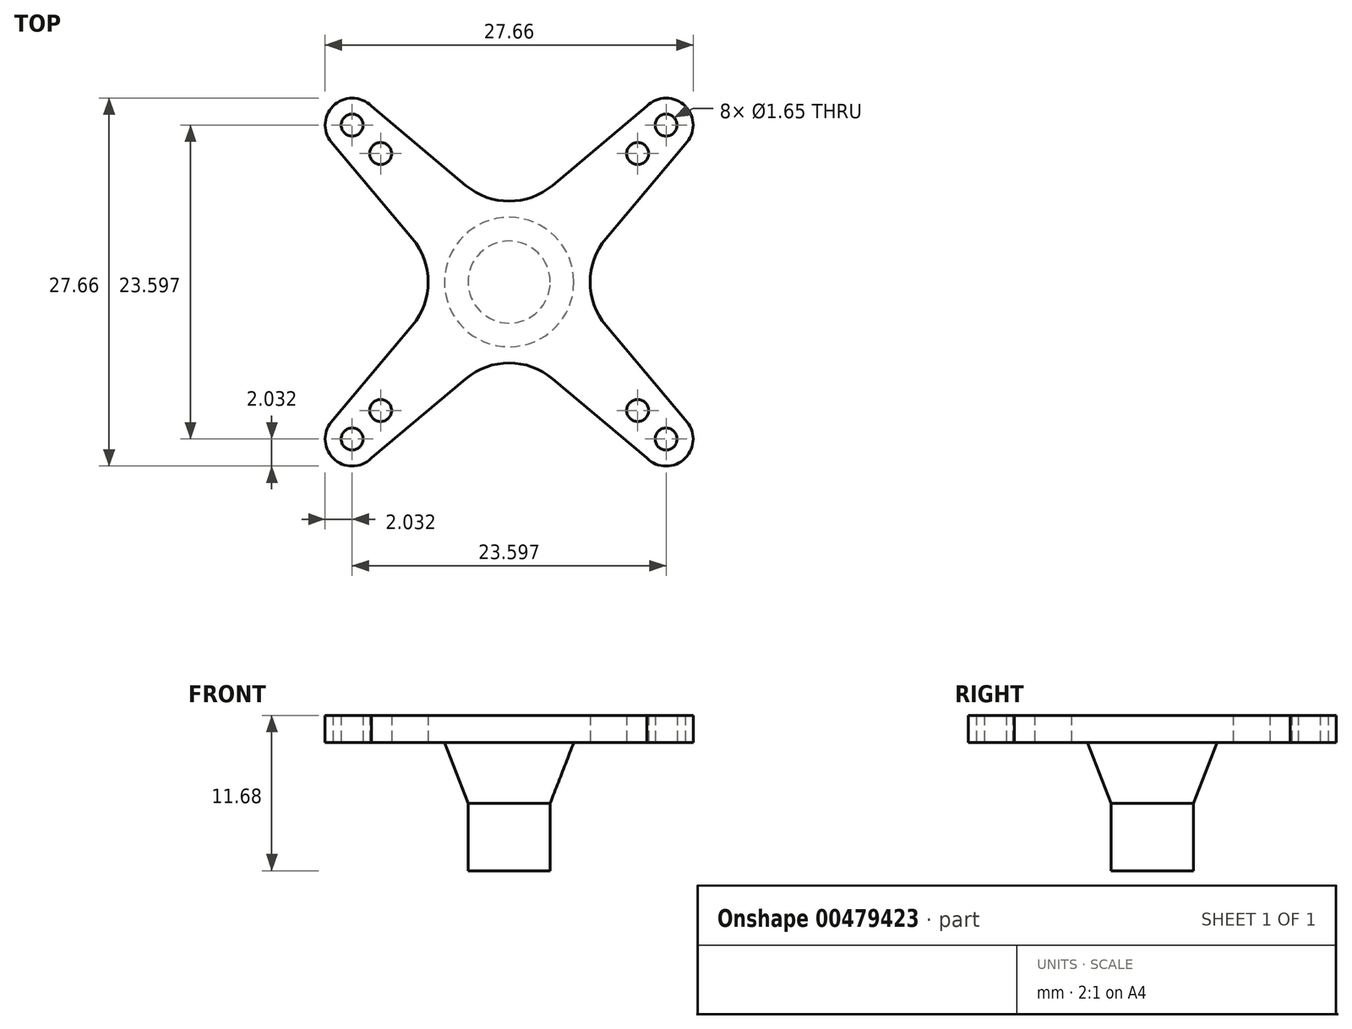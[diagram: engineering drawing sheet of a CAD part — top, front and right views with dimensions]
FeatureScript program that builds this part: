
annotation { "Feature Type Name" : "Feature", "Feature Type Description" : "" }
export const myFeature = defineFeature(function(context is Context, id is Id, definition is map)
    precondition{}
    {
        {
            var Q0;
            Q0=qCreatedBy(makeId("Top.planeOp"),FACE);
            var sketch = newSketch(context, id + "F0", { "sketchPlane" : qUnion([Q0]), "disableImprinting" : false});
            skLineSegment(sketch, "E0", {"start": v(0, 11.16) * mm, "end": v(0, -11.16) * mm});
            skLineSegment(sketch, "E1", {"start": v(11.16, 0) * mm, "end": v(-11.16, 0) * mm});
            skPoint(sketch, "E2", {"position": v(0, 0) * mm});
            skCircle(sketch, "E3", {"center": v(0, 11.16) * mm, "radius": 5.08 * mm});
            skCircle(sketch, "E4", {"center": v(11.16, 0) * mm, "radius": 5.08 * mm});
            skCircle(sketch, "E5", {"center": v(0, -11.16) * mm, "radius": 5.08 * mm});
            skCircle(sketch, "E6", {"center": v(-11.16, 0) * mm, "radius": 5.08 * mm});
            skLineSegment(sketch, "E7", {"start": v(-3.26, 7.27) * mm, "end": v(3.26, 7.27) * mm});
            skLineSegment(sketch, "E8", {"start": v(7.27, 3.26) * mm, "end": v(7.27, -3.26) * mm});
            skLineSegment(sketch, "E9", {"start": v(-3.26, -7.27) * mm, "end": v(3.26, -7.27) * mm});
            skLineSegment(sketch, "E10", {"start": v(-7.27, 3.26) * mm, "end": v(-7.27, -3.26) * mm});
            skLineSegment(sketch, "E11", {"start": v(3.26, -7.27) * mm, "end": v(10.36, -13.24) * mm});
            skLineSegment(sketch, "E12", {"start": v(7.27, -3.26) * mm, "end": v(13.24, -10.36) * mm});
            skLineSegment(sketch, "E13", {"start": v(3.26, 7.27) * mm, "end": v(10.36, 13.24) * mm});
            skLineSegment(sketch, "E14", {"start": v(7.27, 3.26) * mm, "end": v(13.24, 10.36) * mm});
            skLineSegment(sketch, "E15", {"start": v(-7.27, -3.26) * mm, "end": v(-13.24, -10.36) * mm});
            skLineSegment(sketch, "E16", {"start": v(-3.26, -7.27) * mm, "end": v(-10.36, -13.24) * mm});
            skLineSegment(sketch, "E17", {"start": v(-7.27, 3.26) * mm, "end": v(-13.24, 10.36) * mm});
            skLineSegment(sketch, "E18", {"start": v(-3.26, 7.27) * mm, "end": v(-10.36, 13.24) * mm});
            skLineSegment(sketch, "E19", {"start": v(-13.24, 10.36) * mm, "end": v(-10.36, 13.24) * mm});
            skLineSegment(sketch, "E20", {"start": v(10.36, 13.24) * mm, "end": v(13.24, 10.36) * mm});
            skLineSegment(sketch, "E21", {"start": v(13.24, -10.36) * mm, "end": v(10.36, -13.24) * mm});
            skLineSegment(sketch, "E22", {"start": v(-10.36, -13.24) * mm, "end": v(-13.24, -10.36) * mm});
            skPoint(sketch, "E23", {"position": v(-11.8, 11.8) * mm});
            skPoint(sketch, "E24", {"position": v(11.8, 11.8) * mm});
            skPoint(sketch, "E25", {"position": v(11.8, -11.8) * mm});
            skPoint(sketch, "E26", {"position": v(-11.8, -11.8) * mm});
            skCircle(sketch, "E27", {"center": v(-11.8, 11.8) * mm, "radius": 2.03 * mm});
            skCircle(sketch, "E28", {"center": v(11.8, 11.8) * mm, "radius": 2.03 * mm});
            skCircle(sketch, "E29", {"center": v(11.8, -11.8) * mm, "radius": 2.03 * mm});
            skCircle(sketch, "E30", {"center": v(-11.8, -11.8) * mm, "radius": 2.03 * mm});
            skLineSegment(sketch, "E31", {"start": v(-3.26, 7.27) * mm, "end": v(-7.27, 3.26) * mm});
            skLineSegment(sketch, "E32", {"start": v(3.26, 7.27) * mm, "end": v(7.27, 3.26) * mm});
            skLineSegment(sketch, "E33", {"start": v(7.27, -3.26) * mm, "end": v(3.26, -7.27) * mm});
            skLineSegment(sketch, "E34", {"start": v(-7.27, -3.26) * mm, "end": v(-3.26, -7.27) * mm});
            skLineSegment(sketch, "E35", {"start": v(-11.8, 11.8) * mm, "end": v(-5.27, 5.27) * mm});
            skLineSegment(sketch, "E36", {"start": v(11.8, 11.8) * mm, "end": v(5.27, 5.27) * mm});
            skLineSegment(sketch, "E37", {"start": v(11.8, -11.8) * mm, "end": v(5.27, -5.27) * mm});
            skLineSegment(sketch, "E38", {"start": v(-11.8, -11.8) * mm, "end": v(-5.27, -5.27) * mm});
            skCircle(sketch, "E39", {"center": v(-11.8, 11.8) * mm, "radius": 0.83 * mm});
            skCircle(sketch, "E40", {"center": v(11.8, 11.8) * mm, "radius": 0.83 * mm});
            skCircle(sketch, "E41", {"center": v(11.8, -11.8) * mm, "radius": 0.83 * mm});
            skCircle(sketch, "E42", {"center": v(-11.8, -11.8) * mm, "radius": 0.83 * mm});
            skCircle(sketch, "E43", {"center": v(-9.66, 9.66) * mm, "radius": 0.83 * mm});
            skCircle(sketch, "E44", {"center": v(9.66, 9.66) * mm, "radius": 0.83 * mm});
            skCircle(sketch, "E45", {"center": v(-9.66, -9.66) * mm, "radius": 0.83 * mm});
            skCircle(sketch, "E46", {"center": v(9.66, -9.66) * mm, "radius": 0.83 * mm});
            skCircle(sketch, "E47", {"center": v(0, 0) * mm, "radius": 4.86 * mm});
            skSolve(sketch);
        }
        {
            var Q0;
            {var subQ1=sQuery(id+"F0.wireOp",EDGE,"E19");var subQ3=sQuery(id+"F0.wireOp",EDGE,"E39");var subQ4=makeQuery(id+"F0.imprint","INTERSECT",VERTEX,{"disambiguationData":[OD(0.0)],"derivedFrom":[subQ1,subQ3]});Q0=makeQuery(id+"F0.imprint","IMPRINT",FACE,{"disambiguationData":[TD([[makeQuery(id+"F0.imprint","IMPRINT",EDGE,{"disambiguationData":[TD([[subQ4,1.0]])],"derivedFrom":subQ3}),-1.0]])]});}
            var Q1;
            {var subQ1=sQuery(id+"F0.wireOp",EDGE,"E20");var subQ3=sQuery(id+"F0.wireOp",EDGE,"E40");var subQ4=makeQuery(id+"F0.imprint","INTERSECT",VERTEX,{"disambiguationData":[OD(0.0)],"derivedFrom":[subQ1,subQ3]});Q1=makeQuery(id+"F0.imprint","IMPRINT",FACE,{"disambiguationData":[TD([[makeQuery(id+"F0.imprint","IMPRINT",EDGE,{"disambiguationData":[TD([[subQ4,1.0]])],"derivedFrom":subQ3}),-1.0]])]});}
            var Q2;
            {var subQ1=sQuery(id+"F0.wireOp",EDGE,"E21");var subQ3=sQuery(id+"F0.wireOp",EDGE,"E41");var subQ4=makeQuery(id+"F0.imprint","INTERSECT",VERTEX,{"disambiguationData":[OD(0.0)],"derivedFrom":[subQ1,subQ3]});Q2=makeQuery(id+"F0.imprint","IMPRINT",FACE,{"disambiguationData":[TD([[makeQuery(id+"F0.imprint","IMPRINT",EDGE,{"disambiguationData":[TD([[subQ4,1.0]])],"derivedFrom":subQ3}),-1.0]])]});}
            var Q3;
            {var subQ1=sQuery(id+"F0.wireOp",EDGE,"E22");var subQ3=sQuery(id+"F0.wireOp",EDGE,"E42");var subQ4=makeQuery(id+"F0.imprint","INTERSECT",VERTEX,{"disambiguationData":[OD(0.0)],"derivedFrom":[subQ1,subQ3]});Q3=makeQuery(id+"F0.imprint","IMPRINT",FACE,{"disambiguationData":[TD([[makeQuery(id+"F0.imprint","IMPRINT",EDGE,{"disambiguationData":[TD([[subQ4,1.0]])],"derivedFrom":subQ3}),-1.0]])]});}
            var Q4;
            {var subQ0=sQuery(id+"F0.wireOp",EDGE,"E27");var subQ5=sQuery(id+"F0.wireOp",EDGE,"E35");var subQ6=makeQuery(id+"F0.imprint","INTERSECT",VERTEX,{"derivedFrom":[subQ0,subQ5]});Q4=makeQuery(id+"F0.imprint","IMPRINT",FACE,{"disambiguationData":[TD([[makeQuery(id+"F0.imprint","IMPRINT",EDGE,{"disambiguationData":[TD([[subQ6,1.0]])],"derivedFrom":subQ5}),-1.0]])]});}
            var Q5;
            {var subQ0=sQuery(id+"F0.wireOp",EDGE,"E27");var subQ5=sQuery(id+"F0.wireOp",EDGE,"E35");var subQ6=makeQuery(id+"F0.imprint","INTERSECT",VERTEX,{"derivedFrom":[subQ0,subQ5]});Q5=makeQuery(id+"F0.imprint","IMPRINT",FACE,{"disambiguationData":[TD([[makeQuery(id+"F0.imprint","IMPRINT",EDGE,{"disambiguationData":[TD([[subQ6,1.0]])],"derivedFrom":subQ5}),1.0]])]});}
            var Q6;
            {var subQ0=sQuery(id+"F0.wireOp",EDGE,"E28");var subQ5=sQuery(id+"F0.wireOp",EDGE,"E36");var subQ6=makeQuery(id+"F0.imprint","INTERSECT",VERTEX,{"derivedFrom":[subQ0,subQ5]});Q6=makeQuery(id+"F0.imprint","IMPRINT",FACE,{"disambiguationData":[TD([[makeQuery(id+"F0.imprint","IMPRINT",EDGE,{"disambiguationData":[TD([[subQ6,1.0]])],"derivedFrom":subQ5}),-1.0]])]});}
            var Q7;
            {var subQ0=sQuery(id+"F0.wireOp",EDGE,"E28");var subQ5=sQuery(id+"F0.wireOp",EDGE,"E36");var subQ6=makeQuery(id+"F0.imprint","INTERSECT",VERTEX,{"derivedFrom":[subQ0,subQ5]});Q7=makeQuery(id+"F0.imprint","IMPRINT",FACE,{"disambiguationData":[TD([[makeQuery(id+"F0.imprint","IMPRINT",EDGE,{"disambiguationData":[TD([[subQ6,1.0]])],"derivedFrom":subQ5}),1.0]])]});}
            var Q8;
            {var subQ0=sQuery(id+"F0.wireOp",EDGE,"E29");var subQ5=sQuery(id+"F0.wireOp",EDGE,"E37");var subQ6=makeQuery(id+"F0.imprint","INTERSECT",VERTEX,{"derivedFrom":[subQ0,subQ5]});Q8=makeQuery(id+"F0.imprint","IMPRINT",FACE,{"disambiguationData":[TD([[makeQuery(id+"F0.imprint","IMPRINT",EDGE,{"disambiguationData":[TD([[subQ6,1.0]])],"derivedFrom":subQ5}),-1.0]])]});}
            var Q9;
            {var subQ0=sQuery(id+"F0.wireOp",EDGE,"E29");var subQ5=sQuery(id+"F0.wireOp",EDGE,"E37");var subQ6=makeQuery(id+"F0.imprint","INTERSECT",VERTEX,{"derivedFrom":[subQ0,subQ5]});Q9=makeQuery(id+"F0.imprint","IMPRINT",FACE,{"disambiguationData":[TD([[makeQuery(id+"F0.imprint","IMPRINT",EDGE,{"disambiguationData":[TD([[subQ6,1.0]])],"derivedFrom":subQ5}),1.0]])]});}
            var Q10;
            {var subQ0=sQuery(id+"F0.wireOp",EDGE,"E30");var subQ5=sQuery(id+"F0.wireOp",EDGE,"E38");var subQ6=makeQuery(id+"F0.imprint","INTERSECT",VERTEX,{"derivedFrom":[subQ0,subQ5]});Q10=makeQuery(id+"F0.imprint","IMPRINT",FACE,{"disambiguationData":[TD([[makeQuery(id+"F0.imprint","IMPRINT",EDGE,{"disambiguationData":[TD([[subQ6,1.0]])],"derivedFrom":subQ5}),-1.0]])]});}
            var Q11;
            {var subQ0=sQuery(id+"F0.wireOp",EDGE,"E30");var subQ5=sQuery(id+"F0.wireOp",EDGE,"E38");var subQ6=makeQuery(id+"F0.imprint","INTERSECT",VERTEX,{"derivedFrom":[subQ0,subQ5]});Q11=makeQuery(id+"F0.imprint","IMPRINT",FACE,{"disambiguationData":[TD([[makeQuery(id+"F0.imprint","IMPRINT",EDGE,{"disambiguationData":[TD([[subQ6,1.0]])],"derivedFrom":subQ5}),1.0]])]});}
            var Q12;
            {var subQ6=sQuery(id+"F0.wireOp",EDGE,"E18");Q12=makeQuery(id+"F0.imprint","IMPRINT",FACE,{"disambiguationData":[TD([[makeQuery(id+"F0.imprint","IMPRINT",EDGE,{"derivedFrom":subQ6}),1.0]])]});}
            var Q13;
            {var subQ6=sQuery(id+"F0.wireOp",EDGE,"E13");Q13=makeQuery(id+"F0.imprint","IMPRINT",FACE,{"disambiguationData":[TD([[makeQuery(id+"F0.imprint","IMPRINT",EDGE,{"derivedFrom":subQ6}),-1.0]])]});}
            var Q14;
            {var subQ6=sQuery(id+"F0.wireOp",EDGE,"E14");Q14=makeQuery(id+"F0.imprint","IMPRINT",FACE,{"disambiguationData":[TD([[makeQuery(id+"F0.imprint","IMPRINT",EDGE,{"derivedFrom":subQ6}),1.0]])]});}
            var Q15;
            {var subQ0=sQuery(id+"F0.wireOp",EDGE,"E12");Q15=makeQuery(id+"F0.imprint","IMPRINT",FACE,{"disambiguationData":[TD([[makeQuery(id+"F0.imprint","IMPRINT",EDGE,{"derivedFrom":subQ0}),-1.0]])]});}
            var Q16;
            {var subQ6=sQuery(id+"F0.wireOp",EDGE,"E11");Q16=makeQuery(id+"F0.imprint","IMPRINT",FACE,{"disambiguationData":[TD([[makeQuery(id+"F0.imprint","IMPRINT",EDGE,{"derivedFrom":subQ6}),1.0]])]});}
            var Q17;
            {var subQ6=sQuery(id+"F0.wireOp",EDGE,"E16");Q17=makeQuery(id+"F0.imprint","IMPRINT",FACE,{"disambiguationData":[TD([[makeQuery(id+"F0.imprint","IMPRINT",EDGE,{"derivedFrom":subQ6}),-1.0]])]});}
            var Q18;
            {var subQ8=sQuery(id+"F0.wireOp",EDGE,"E17");Q18=makeQuery(id+"F0.imprint","IMPRINT",FACE,{"disambiguationData":[TD([[makeQuery(id+"F0.imprint","IMPRINT",EDGE,{"derivedFrom":subQ8}),-1.0]])]});}
            var Q19;
            {var subQ6=sQuery(id+"F0.wireOp",EDGE,"E15");Q19=makeQuery(id+"F0.imprint","IMPRINT",FACE,{"disambiguationData":[TD([[makeQuery(id+"F0.imprint","IMPRINT",EDGE,{"derivedFrom":subQ6}),1.0]])]});}
            var Q20;
            {var subQ5=sQuery(id+"F0.wireOp",EDGE,"E3");var subQ7=sQuery(id+"F0.wireOp",EDGE,"E0");var subQ8=makeQuery(id+"F0.imprint","INTERSECT",VERTEX,{"derivedFrom":[subQ7,subQ5]});Q20=makeQuery(id+"F0.imprint","IMPRINT",FACE,{"disambiguationData":[TD([[makeQuery(id+"F0.imprint","IMPRINT",EDGE,{"disambiguationData":[TD([[subQ8,-1.0]])],"derivedFrom":subQ7}),1.0]])]});}
            var Q21;
            {var subQ5=sQuery(id+"F0.wireOp",EDGE,"E3");var subQ6=sQuery(id+"F0.wireOp",EDGE,"E0");var subQ7=makeQuery(id+"F0.imprint","INTERSECT",VERTEX,{"derivedFrom":[subQ6,subQ5]});Q21=makeQuery(id+"F0.imprint","IMPRINT",FACE,{"disambiguationData":[TD([[makeQuery(id+"F0.imprint","IMPRINT",EDGE,{"disambiguationData":[TD([[subQ7,-1.0]])],"derivedFrom":subQ6}),-1.0]])]});}
            var Q22;
            {var subQ3=sQuery(id+"F0.wireOp",EDGE,"E0");var subQ5=sQuery(id+"F0.wireOp",EDGE,"E1");var subQ6=makeQuery(id+"F0.imprint","INTERSECT",VERTEX,{"derivedFrom":[subQ3,subQ5]});Q22=makeQuery(id+"F0.imprint","IMPRINT",FACE,{"disambiguationData":[TD([[makeQuery(id+"F0.imprint","IMPRINT",EDGE,{"disambiguationData":[TD([[subQ6,-1.0]])],"derivedFrom":subQ3}),-1.0]])]});}
            var Q23;
            {var subQ3=sQuery(id+"F0.wireOp",EDGE,"E0");var subQ7=sQuery(id+"F0.wireOp",EDGE,"E1");var subQ9=makeQuery(id+"F0.imprint","INTERSECT",VERTEX,{"derivedFrom":[subQ3,subQ7]});Q23=makeQuery(id+"F0.imprint","IMPRINT",FACE,{"disambiguationData":[TD([[makeQuery(id+"F0.imprint","IMPRINT",EDGE,{"disambiguationData":[TD([[subQ9,-1.0]])],"derivedFrom":subQ3}),1.0]])]});}
            var Q24;
            {var subQ3=sQuery(id+"F0.wireOp",EDGE,"E0");var subQ8=sQuery(id+"F0.wireOp",EDGE,"E47");var subQ11=makeQuery(id+"F0.imprint","INTERSECT",VERTEX,{"disambiguationData":[OD(1.0)],"derivedFrom":[subQ3,subQ8]});Q24=makeQuery(id+"F0.imprint","IMPRINT",FACE,{"disambiguationData":[TD([[makeQuery(id+"F0.imprint","IMPRINT",EDGE,{"disambiguationData":[TD([[subQ11,-1.0]])],"derivedFrom":subQ3}),1.0]])]});}
            var Q25;
            {var subQ5=sQuery(id+"F0.wireOp",EDGE,"E47");var subQ9=sQuery(id+"F0.wireOp",EDGE,"E0");var subQ11=makeQuery(id+"F0.imprint","INTERSECT",VERTEX,{"disambiguationData":[OD(1.0)],"derivedFrom":[subQ9,subQ5]});Q25=makeQuery(id+"F0.imprint","IMPRINT",FACE,{"disambiguationData":[TD([[makeQuery(id+"F0.imprint","IMPRINT",EDGE,{"disambiguationData":[TD([[subQ11,-1.0]])],"derivedFrom":subQ9}),-1.0]])]});}
            var Q26;
            {var subQ0=sQuery(id+"F0.wireOp",EDGE,"E47");var subQ1=sQuery(id+"F0.wireOp",EDGE,"E0");var subQ2=makeQuery(id+"F0.imprint","INTERSECT",VERTEX,{"disambiguationData":[OD(0.0)],"derivedFrom":[subQ1,subQ0]});Q26=makeQuery(id+"F0.imprint","IMPRINT",FACE,{"disambiguationData":[TD([[makeQuery(id+"F0.imprint","IMPRINT",EDGE,{"disambiguationData":[TD([[subQ2,-1.0]])],"derivedFrom":subQ1}),-1.0]])]});}
            var Q27;
            {var subQ0=sQuery(id+"F0.wireOp",EDGE,"E47");var subQ1=sQuery(id+"F0.wireOp",EDGE,"E0");var subQ2=makeQuery(id+"F0.imprint","INTERSECT",VERTEX,{"disambiguationData":[OD(0.0)],"derivedFrom":[subQ1,subQ0]});Q27=makeQuery(id+"F0.imprint","IMPRINT",FACE,{"disambiguationData":[TD([[makeQuery(id+"F0.imprint","IMPRINT",EDGE,{"disambiguationData":[TD([[subQ2,-1.0]])],"derivedFrom":subQ1}),1.0]])]});}
            extrude(context, id + "F1", {"entities" : qUnion([Q0, Q1, Q2, Q3, Q4, Q5, Q6, Q7, Q8, Q9, Q10, Q11, Q12, Q13, Q14, Q15, Q16, Q17, Q18, Q19, Q20, Q21, Q22, Q23, Q24, Q25, Q26, Q27]), "depth" : 2.03 * mm, "offsetDistance" : 25.4 * mm});
        }
        {
            var Q0;
            {var subQ0=sQuery(id+"F0.wireOp",EDGE,"E47");var subQ1=sQuery(id+"F0.wireOp",EDGE,"E0");var subQ2=makeQuery(id+"F0.imprint","INTERSECT",VERTEX,{"disambiguationData":[OD(0.0)],"derivedFrom":[subQ1,subQ0]});Q0=makeQuery(id+"F0.imprint","IMPRINT",FACE,{"disambiguationData":[TD([[makeQuery(id+"F0.imprint","IMPRINT",EDGE,{"disambiguationData":[TD([[subQ2,-1.0]])],"derivedFrom":subQ1}),-1.0]])]});}
            var Q1;
            {var subQ0=sQuery(id+"F0.wireOp",EDGE,"E1");var subQ1=sQuery(id+"F0.wireOp",EDGE,"E0");var subQ2=makeQuery(id+"F0.imprint","INTERSECT",VERTEX,{"derivedFrom":[subQ1,subQ0]});Q1=makeQuery(id+"F0.imprint","IMPRINT",FACE,{"disambiguationData":[TD([[makeQuery(id+"F0.imprint","IMPRINT",EDGE,{"disambiguationData":[TD([[subQ2,-1.0]])],"derivedFrom":subQ1}),1.0]])]});}
            var Q2;
            {var subQ0=sQuery(id+"F0.wireOp",EDGE,"E47");var subQ1=sQuery(id+"F0.wireOp",EDGE,"E0");var subQ2=makeQuery(id+"F0.imprint","INTERSECT",VERTEX,{"disambiguationData":[OD(0.0)],"derivedFrom":[subQ1,subQ0]});Q2=makeQuery(id+"F0.imprint","IMPRINT",FACE,{"disambiguationData":[TD([[makeQuery(id+"F0.imprint","IMPRINT",EDGE,{"disambiguationData":[TD([[subQ2,-1.0]])],"derivedFrom":subQ1}),1.0]])]});}
            var Q3;
            {var subQ0=sQuery(id+"F0.wireOp",EDGE,"E1");var subQ1=sQuery(id+"F0.wireOp",EDGE,"E0");var subQ2=makeQuery(id+"F0.imprint","INTERSECT",VERTEX,{"derivedFrom":[subQ1,subQ0]});Q3=makeQuery(id+"F0.imprint","IMPRINT",FACE,{"disambiguationData":[TD([[makeQuery(id+"F0.imprint","IMPRINT",EDGE,{"disambiguationData":[TD([[subQ2,-1.0]])],"derivedFrom":subQ1}),-1.0]])]});}
            extrude(context, id + "F2", {"entities" : qUnion([Q0, Q1, Q2, Q3]), "operationType" : NewBodyOperationType.ADD, "oppositeDirection" : true, "depth" : 4.57 * mm, "offsetDistance" : 25.4 * mm});
        }
        {
            var Q0;
            Q0=makeQuery(id+"F2.opExtrude","CAP_EDGE",EDGE,{"disambiguationData":[OSD([sQuery(id+"F0.wireOp",EDGE,"E47")])],"isStart":false});
            chamfer(context, id + "F3", {"entities" : qUnion([Q0]), "chamferType" : ChamferType.TWO_OFFSETS, "width1" : 4.57 * mm, "oppositeDirection" : false, "width2" : 1.78 * mm, "tangentPropagation" : true});
        }
        {
            var Q0;
            Q0=makeQuery(id+"F2.opExtrude","CAP_FACE",FACE,{"disambiguationData":[OSD([sQuery(id+"F0.wireOp",EDGE,"E47")])],"isStart":false});
            extrude(context, id + "F4", {"entities" : qUnion([Q0]), "operationType" : NewBodyOperationType.ADD, "depth" : 5.08 * mm, "offsetDistance" : 25.4 * mm});
        }
    });
